# Revit family: 41750
name_source: partatom
category: Lighting Fixtures
revit_build: Autodesk Revit 2018 (Build: 20170223_1515(x64)
units: mm (PartAtom-declared; Revit-internal decimal feet)

## family parameters
Cut with Voids When Loaded = No
Host = Face
Light Source = No
OmniClass Number = 23.80.70.00
OmniClass Title = Lighting
Part Type = Normal
Room Calculation Point = No
Round Connector Dimension = Use Diameter
Shared = No

## types (1)
- 0041750 SYLSAFE EXIT-MOD EX R EM3 MT DA
    Apparent Load = 5 VA
    Assembly Code = D5020200
    AssetType = Fixed
    ClassificationName = Uniclass2015
    ClassificationValue = EF_70_80
    Cost = 0 $
    Default Elevation = 1219 mm
    Description = SylSafe Exit-Mod EX R EM3 MT DA is a recessed emergency exit sign. Comes with ISO7010 compliant legend pack. Arrows left, right, up, down and a blank sheet for single sided versions. EC legend pack is available as accessory. Viewing distance 26m. White housing colour.  Maintained 3hr emergency operation with NiMH rechargeable battery. Recharge period 24 hours. Self testing with DALI monitoring capability. 4.9W, IK03, IP20. Power Factor 0.49. Class II electrical construction.
    DocumentationLiterature = http://www.sylvania-lighting.com
    DurationUnit = hours
    ElectricShockClassification = 0
    ExpectedLife = 50000
    IfcExportAs = Class II
    IfcExportType = IfcLightFixtureType
    ImpactProtectionIndex = IfcLightFixtureType
    IngressProtection = IfcLightFixtureType
    InputNominalFrequency = 0
    InputVoltage = 0
    LampColourRenderingIndex = 16500
    LampColourTemperature = LED
    LampMacAdamStep = 0
    LampNominalLuminous = 0 K
    Length_SYL = 308 mm  [stored 1.0105 ft]
    LightOutputRatio = LED
    LuminaireType = 0
    ManufacturerName = 0 lm/W
    Material = Feilo Sylvania
    Material_1_SYL = PC/ABS Plastic
    Material_2_SYL = <By Category>
    Material_3_SYL = <By Category>
    Material_4_SYL = <By Category>
    Model = SylSafe Exit-Mod EX R EM3 MT DA
    ModelNumber = 0041750
    ModelReference = SylSafe Exit-Mod EX R EM3 MT DA
    Name = SylSafe Exit-Mod EX R EM3 MT DA
    NominalDepth = 18 mm  [stored 0.0590551 ft]
    NominalHeight = 234 mm  [stored 0.767717 ft]
    NominalLength = 49 mm  [stored 0.160761 ft]
    PowerConsumption = Lighting
    PowerFactor = 0.6
    RadiusBody_SYL = 17 mm  [stored 0.0557743 ft]
    RotatableArmThickness_SYL = 3 mm  [stored 0.00984252 ft]
    Type Image = <None>
    TypeName = SylSafe Exit-Mod EX R EM3 MT DA
    TypeSign_SYL = SylSafe EXIT Sign : Exit Arrow Down
    URL = 0.49
    Voltage = 0 V
    WarrantyDescription = http://www.sylvania-lighting.com
    Width_SYL = 34 mm  [stored 0.111549 ft]

note: [stored X ft] marks values corroborated as IEEE doubles in the binary element streams (Revit-internal decimal feet)

## geometry (parser evidence)
native form markers: Sweep x4
no freeform markers — native parametric forms only
